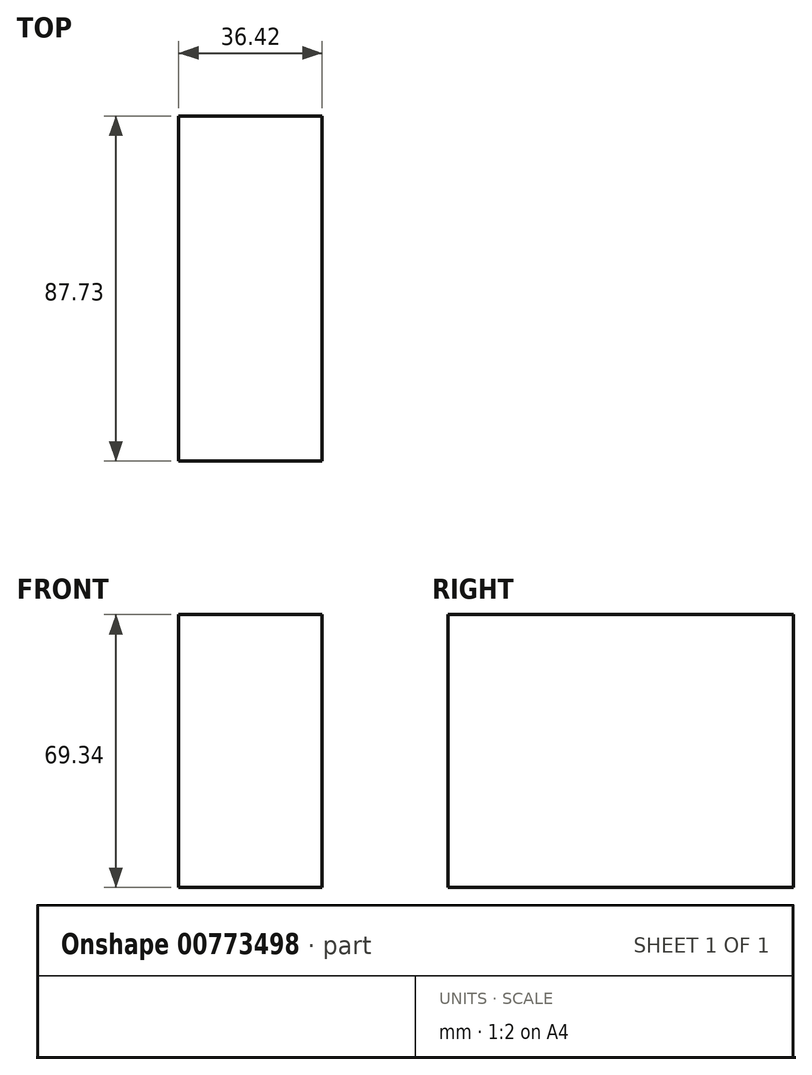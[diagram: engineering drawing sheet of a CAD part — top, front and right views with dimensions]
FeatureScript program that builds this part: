
annotation { "Feature Type Name" : "Feature", "Feature Type Description" : "" }
export const myFeature = defineFeature(function(context is Context, id is Id, definition is map)
    precondition{}
    {
        {
            var Q0;
            Q0=qCreatedBy(makeId("Top.planeOp"),FACE);
            var sketch = newSketch(context, id + "F0", { "sketchPlane" : qUnion([Q0])});
            skLineSegment(sketch, "E0.bottom", {"start": v(-127, -75) * mm, "end": v(-90.58, -75) * mm});
            skLineSegment(sketch, "E0.top", {"start": v(-127, 12.74) * mm, "end": v(-90.58, 12.74) * mm});
            skLineSegment(sketch, "E0.left", {"start": v(-127, -75) * mm, "end": v(-127, 12.74) * mm});
            skLineSegment(sketch, "E0.right", {"start": v(-90.58, -75) * mm, "end": v(-90.58, 12.74) * mm});
            skSolve(sketch);
        }
        {
            var Q0;
            Q0=makeQuery(id+"F0.imprint","IMPRINT",FACE,{"disambiguationData":[TD([[makeQuery(id+"F0.imprint","IMPRINT",EDGE,{"derivedFrom":sQuery(id+"F0.wireOp",EDGE,"E0.bottom")}),1.0]])]});
            extrude(context, id + "F1", {"entities" : qUnion([Q0]), "depth" : 69.34 * mm, "offsetDistance" : 25.4 * mm});
        }
    });
